# Revit family: EKF_EE_ШирокаяРейкаБоковаяTrivia_AVERES
name_source: partatom
category: Электрооборудование
units: mm (PartAtom-declared; Revit-internal decimal feet)

## family parameters
Всегда вертикально = Нет
На основе рабочей плоскости = Да
Общий = Да
При загрузке вырезать с полостями = Нет
Размер круглого соединителя = Использовать диаметр
Тип детали = Силовой щит
Точка расчета площади = Нет

## types (3) — shared parameters
ADSK_Единица измерения = шт.
ADSK_Завод-изготовитель = EKF
ADSK_Количество = 1
ADSK_Размер_Высота = 76 мм
ADSK_Размер_Глубина = 23 мм
t1 = 2 мм
Высота = 76 мм
Глубина = 23 мм
Изготовитель = EKF
Отступ = 3.5 мм
Серия номенклатуры = Averes
Степень защиты IP = -
ТВ = EKF_2_TRIVIA_AVERES
Тип установки = -
Шаг = 25 мм
zero-valued in all types: ADSK_Масса, Отметка по умолчанию

## per-type parameters (varying)
| type | ADSK_Код изделия | ADSK_Марка | ADSK_Наименование | ADSK_Обозначение | ADSK_Размер_Ширина | КоличествоКв | КоличествоКр | ОтступВырез | Тип | Ширина |
| Широкая рейка боковая Д800 (4шт) EKF AVERES | ARW800 | Широкая рейка боковая Д800 (4 шт) EKF AVERES | Широкая рейка боковая Д800 (4 шт) EKF AVERES | Широкая рейка боковая Д800 (4 шт) EKF AVERES | 698 мм | 28 | 27 | 11.5 мм | 688 мм | 698 мм |
| Широкая рейка боковая Д600 (4шт) EKF AVERES | ARW600 | Широкая рейка боковая Д600 (4 шт) EKF AVERES | Широкая рейка боковая Д600 (4 шт) EKF AVERES | Широкая рейка боковая Д600 (4 шт) EKF AVERES | 498 мм | 20 | 19 | 11.5 мм | 687 мм | 498 мм |
| Широкая рейка боковая Д400 (4шт) EKF AVERES | ARW400 | Широкая рейка боковая Д400 (4 шт) EKF AVERES | Широкая рейка боковая Д400 (4 шт) EKF AVERES | Широкая рейка боковая Д400 (4 шт) EKF AVERES | 299 мм | 12 | 11 | 12 мм | 686 мм | 299 мм |
